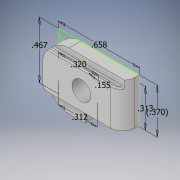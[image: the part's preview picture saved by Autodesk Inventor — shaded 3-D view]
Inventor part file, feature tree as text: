
AUTODESK INVENTOR PART (.ipt)
format: ipt  version: 2018.3 (Build 223284000, 284)  size: 175,616 bytes
history: native  units: in
note: dims shown in document units (in); Inventor stores cm internally (conversion verified against a paired STEP export)
features: fillet x3, extrude x2, sketch x1, chamfer x1
ambient origin geometry x8: Origin, YZ Plane, XZ Plane, XY Plane, X Axis, Y Axis, Z Axis, Center Point
bodies: Solid1 (feature_tree)
feature tree (7):
  sketch  "Sketch1"  dims[d0=0.658in d3=0.312in d4=0.37in d5=0.467in d6=0.32in d7=0.155in d8=0.0985in d9=0.0in d10=0.313in d13=0.136in d14=0.0in d16=0.1in d17=0.01in d18=0.18in d19=0.02in d20=0.0625in d21=45.0deg]
  extrude  "Extrusion1"  Depth=0.18in
  extrude  "Extrusion3"  Depth=0.18in
  fillet  "Fillet2"  Radius=0.467in
  fillet  "Fillet3"  Radius=0.32in
  fillet  "Fillet4"  Radius=0.155in
  chamfer  "Chamfer1"  Distance=0.0985in
